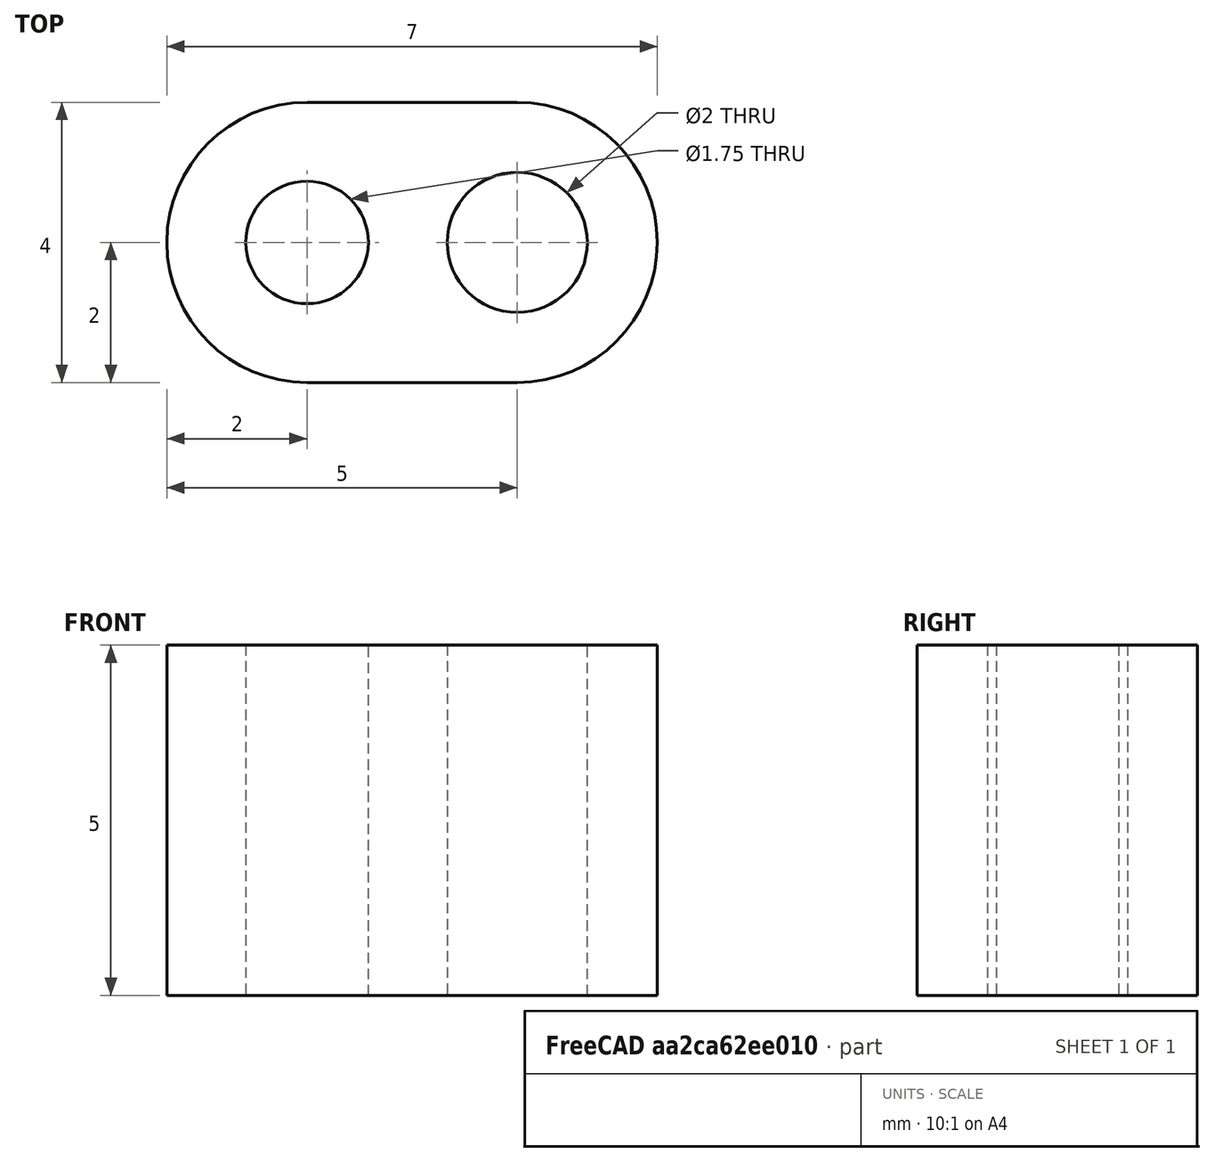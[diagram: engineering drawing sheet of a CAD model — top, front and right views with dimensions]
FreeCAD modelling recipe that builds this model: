
FCSTD DOCUMENT  (FreeCAD 0.18R14555 (Git shallow))
Label: filament-clip
License: All rights reserved
LicenseURL: http://en.wikipedia.org/wiki/All_rights_reserved
objects: Sketcher::SketchObject×1, PartDesign::Pad×1, PartDesign::Body×1
note: 4 computed .brp shape members not serialized (recipe doc carries the construction recipe); baked Part::Feature solids carry a one-line shape summary decoded from their .brp

FEATURE [Sketcher::SketchObject] Sketch
  MapMode = 5
  Support = -> [XY_Plane]
  sketch-geometry (7):
    g0: Circle CenterX=0 CenterY=0 CenterZ=0 NormalX=0 NormalY=0 NormalZ=1 AngleXU=0 Radius=0.875
    g1: Circle CenterX=3 CenterY=0 CenterZ=0 NormalX=0 NormalY=0 NormalZ=1 AngleXU=0 Radius=1
    g2: LineSegment [constr] StartX=3 StartY=0 StartZ=0 EndX=0 EndY=0 EndZ=0
    g3: ArcOfCircle CenterX=0 CenterY=0 CenterZ=0 NormalX=0 NormalY=0 NormalZ=1 AngleXU=0 Radius=2 StartAngle=1.5708 EndAngle=4.71239
    g4: ArcOfCircle CenterX=3 CenterY=0 CenterZ=0 NormalX=0 NormalY=0 NormalZ=1 AngleXU=0 Radius=2 StartAngle=4.71239 EndAngle=7.85398
    g5: LineSegment StartX=3 StartY=2 StartZ=0 EndX=-8.9488e-12 EndY=2 EndZ=0
    g6: LineSegment StartX=0 StartY=-2 StartZ=0 EndX=3 EndY=-2 EndZ=0
  constraints (15):
    c: Coincident(g2,g1)
    c: Coincident(g2,g0)
    c: Horizontal(g2)
    c: Coincident(g3,g0)
    c: Coincident(g4,g1)
    c: Horizontal(g6)
    c: Radius(g0) = 0.875
    c: Tangent(g5,g3) = -1.5708
    c: Tangent(g6,g3) = -1.5708
    c: Tangent(g5,g4) = -1.5708
    c: Tangent(g6,g4) = -1.5708
    c: Radius(g3) = 2
    c: DistanceX(g2,g2) = 3
    c: Coincident(g0,g-1)
    c: Radius(g1) = 1
FEATURE [PartDesign::Pad] Pad
  Length = 5
  Length2 = 100
  Profile = -> Sketch
  Type = 0
FEATURE [PartDesign::Body] Body
  Group = -> [Sketch,Pad]
  Origin = -> Origin
  Tip = -> Pad
